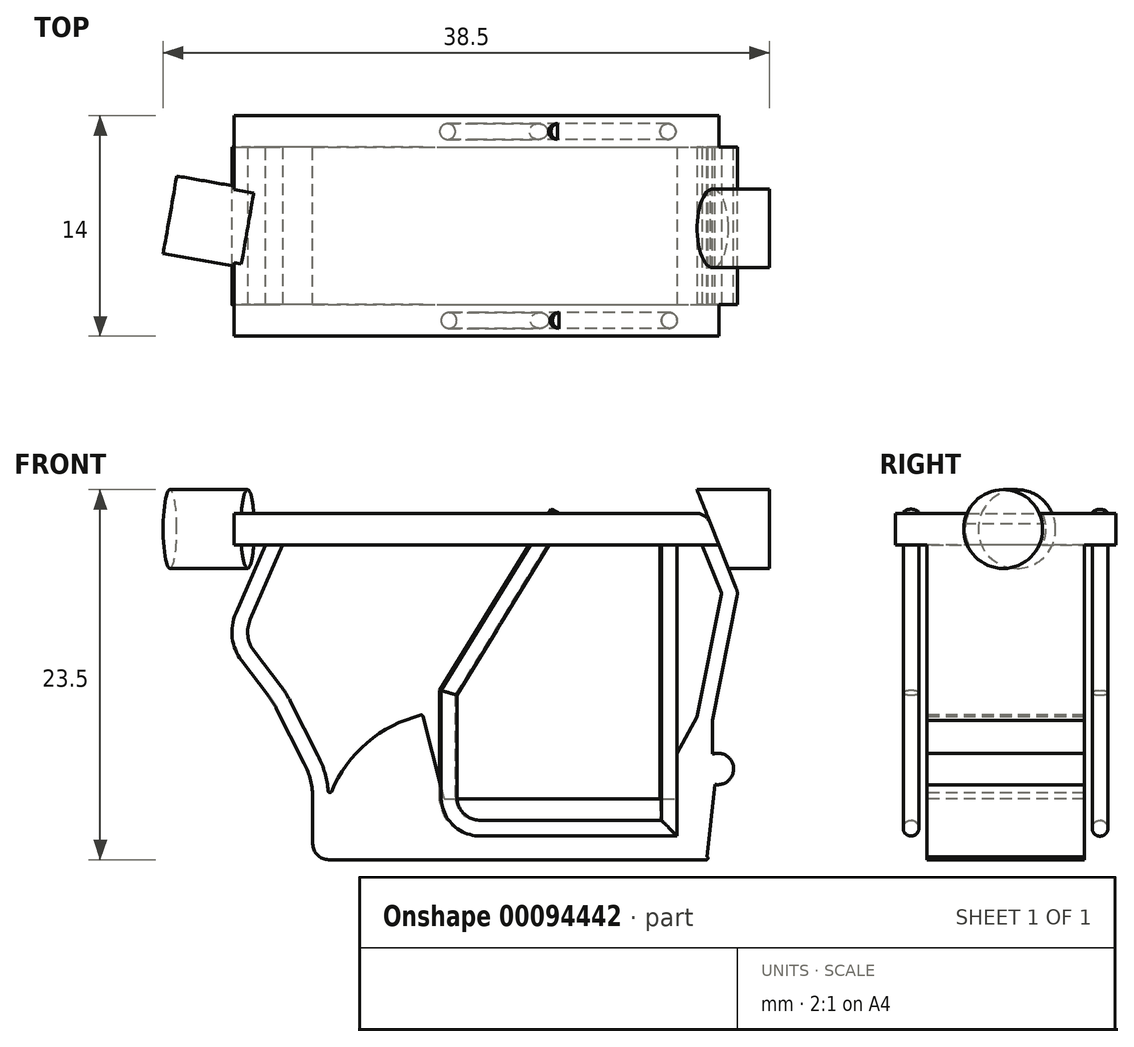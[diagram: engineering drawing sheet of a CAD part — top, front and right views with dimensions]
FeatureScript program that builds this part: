
annotation { "Feature Type Name" : "Feature", "Feature Type Description" : "" }
export const myFeature = defineFeature(function(context is Context, id is Id, definition is map)
    precondition{}
    {
        {
            var Q0;
            Q0=qCreatedBy(makeId("Front.planeOp"),FACE);
            var sketch = newSketch(context, id + "F0", { "sketchPlane" : qUnion([Q0])});
            skLineSegment(sketch, "E0", {"start": v(0, 1) * mm, "end": v(0, 3.86) * mm});
            skLineSegment(sketch, "E1", {"start": v(-4.89, 15.66) * mm, "end": v(-3, 20) * mm});
            skLineSegment(sketch, "E2", {"start": v(-3, 20) * mm, "end": v(-5, 20) * mm});
            skLineSegment(sketch, "E3", {"start": v(-5, 20) * mm, "end": v(-5, 22) * mm});
            skLineSegment(sketch, "E4", {"start": v(-5, 22) * mm, "end": v(24.32, 22) * mm});
            skLineSegment(sketch, "E5", {"start": v(25.25, 21.37) * mm, "end": v(26.9, 17.27) * mm});
            skLineSegment(sketch, "E6", {"start": v(26.94, 16.7) * mm, "end": v(25.4, 8.86) * mm});
            skLineSegment(sketch, "E7", {"start": v(1, 0) * mm, "end": v(25, 0) * mm});
            skLineSegment(sketch, "E8", {"start": v(-0.54, 6.13) * mm, "end": v(-2.32, 9.62) * mm});
            skLineSegment(sketch, "E9", {"start": v(-2.8, 10.39) * mm, "end": v(-4.52, 12.64) * mm});
            skPoint(sketch, "E10.visualSharp", {"position": v(0, 5.06) * mm});
            skArc(sketch, "E10.filletArc", {"start": v(0, 3.86) * mm, "mid": v(-0.14, 5.03) * mm, "end": v(-0.54, 6.13) * mm});
            skPoint(sketch, "E11.visualSharp", {"position": v(-2.52, 10.03) * mm});
            skArc(sketch, "E11.filletArc", {"start": v(-2.32, 9.62) * mm, "mid": v(-2.54, 10.02) * mm, "end": v(-2.8, 10.39) * mm});
            skPoint(sketch, "E12.visualSharp", {"position": v(-5.59, 14.04) * mm});
            skArc(sketch, "E12.filletArc", {"start": v(-4.89, 15.66) * mm, "mid": v(-5.11, 14.1) * mm, "end": v(-4.52, 12.64) * mm});
            skPoint(sketch, "E13.visualSharp", {"position": v(0, 0) * mm});
            skArc(sketch, "E13.filletArc", {"start": v(0, 1) * mm, "mid": v(0.3, 0.3) * mm, "end": v(1, 0) * mm});
            skPoint(sketch, "E14.visualSharp", {"position": v(25, 22) * mm});
            skArc(sketch, "E14.filletArc", {"start": v(25.25, 21.37) * mm, "mid": v(24.88, 21.83) * mm, "end": v(24.32, 22) * mm});
            skPoint(sketch, "E15.visualSharp", {"position": v(27, 17) * mm});
            skArc(sketch, "E15.filletArc", {"start": v(26.94, 16.7) * mm, "mid": v(26.96, 17) * mm, "end": v(26.9, 17.27) * mm});
            skPoint(sketch, "E16.visualSharp", {"position": v(30, 0) * mm});
            skArc(sketch, "E16.filletArc", {"start": v(25, 0) * mm, "mid": v(25.1, 0.08) * mm, "end": v(25.05, 0.2) * mm});
            skLineSegment(sketch, "E17", {"start": v(25.4, 8.86) * mm, "end": v(25.4, 6.7) * mm});
            skLineSegment(sketch, "E18", {"start": v(25.05, 0.2) * mm, "end": v(25.53, 4.78) * mm});
            skArc(sketch, "E19", {"start": v(25.53, 4.78) * mm, "mid": v(26.73, 5.84) * mm, "end": v(25.4, 6.7) * mm});
            skSolve(sketch);
        }
        {
            var Q0;
            Q0=makeQuery(id+"F0.imprint","IMPRINT",FACE,{"disambiguationData":[TD([[makeQuery(id+"F0.imprint","IMPRINT",EDGE,{"derivedFrom":sQuery(id+"F0.wireOp",EDGE,"E0")}),-1.0]])]});
            extrude(context, id + "F1", {"entities" : qUnion([Q0]), "depth" : 10 * mm});
        }
        {
            var Q0;
            Q0=makeQuery(id+"F1.opExtrude","CAP_FACE",FACE,{"disambiguationData":[OSD([sQuery(id+"F0.wireOp",EDGE,"E0"),sQuery(id+"F0.wireOp",EDGE,"E1"),sQuery(id+"F0.wireOp",EDGE,"E2"),sQuery(id+"F0.wireOp",EDGE,"E3"),sQuery(id+"F0.wireOp",EDGE,"E4"),sQuery(id+"F0.wireOp",EDGE,"E5"),sQuery(id+"F0.wireOp",EDGE,"E6"),sQuery(id+"F0.wireOp",EDGE,"E7"),sQuery(id+"F0.wireOp",EDGE,"E8"),sQuery(id+"F0.wireOp",EDGE,"E9"),sQuery(id+"F0.wireOp",EDGE,"E10.filletArc"),sQuery(id+"F0.wireOp",EDGE,"E11.filletArc"),sQuery(id+"F0.wireOp",EDGE,"E12.filletArc"),sQuery(id+"F0.wireOp",EDGE,"E13.filletArc"),sQuery(id+"F0.wireOp",EDGE,"E14.filletArc"),sQuery(id+"F0.wireOp",EDGE,"E15.filletArc"),sQuery(id+"F0.wireOp",EDGE,"E16.filletArc"),sQuery(id+"F0.wireOp",EDGE,"E17"),sQuery(id+"F0.wireOp",EDGE,"E18"),sQuery(id+"F0.wireOp",EDGE,"E19")])],"isStart":false});
            var sketch = newSketch(context, id + "F2", { "sketchPlane" : qUnion([Q0])});
            skLineSegment(sketch, "E20", {"start": v(-5, 20) * mm, "end": v(25.8, 20) * mm});
            skLineSegment(sketch, "E21.0", {"start": v(-3.97, 15.26) * mm, "end": v(-2.08, 19.6) * mm});
            skArc(sketch, "E21.1", {"start": v(-3.97, 15.26) * mm, "mid": v(-4.12, 14.22) * mm, "end": v(-3.73, 13.25) * mm});
            skArc(sketch, "E21.2", {"start": v(0.98, 4.35) * mm, "mid": v(0.77, 5.5) * mm, "end": v(0.35, 6.58) * mm});
            skLineSegment(sketch, "E21.3", {"start": v(0.35, 6.58) * mm, "end": v(-1.43, 10.08) * mm});
            skArc(sketch, "E21.4", {"start": v(-1.43, 10.08) * mm, "mid": v(-1.7, 10.55) * mm, "end": v(-2, 11) * mm});
            skLineSegment(sketch, "E21.5", {"start": v(-2, 11) * mm, "end": v(-3.73, 13.25) * mm});
            skLineSegment(sketch, "E22", {"start": v(-2.08, 19.6) * mm, "end": v(-1.9, 20) * mm});
            skArc(sketch, "E23.0", {"start": v(26.94, 16.7) * mm, "mid": v(26.96, 17) * mm, "end": v(26.9, 17.27) * mm});
            skLineSegment(sketch, "E24.0", {"start": v(25.96, 16.87) * mm, "end": v(24.41, 9.06) * mm});
            skLineSegment(sketch, "E25", {"start": v(25.95, 16.93) * mm, "end": v(24.72, 20) * mm});
            skArc(sketch, "E26.filletArc", {"start": v(25.96, 16.87) * mm, "mid": v(25.96, 16.9) * mm, "end": v(25.95, 16.93) * mm});
            skArc(sketch, "E27", {"start": v(6.88, 9.18) * mm, "mid": v(3.45, 7.42) * mm, "end": v(1.18, 4.32) * mm});
            skLineSegment(sketch, "E28", {"start": v(7, 9.1) * mm, "end": v(8.31, 3.94) * mm});
            skLineSegment(sketch, "E29", {"start": v(23.12, 6.71) * mm, "end": v(24.41, 9.06) * mm});
            skPoint(sketch, "E30.visualSharp", {"position": v(1, 3.86) * mm});
            skArc(sketch, "E30.filletArc", {"start": v(0.98, 4.35) * mm, "mid": v(1.07, 4.26) * mm, "end": v(1.18, 4.32) * mm});
            skPoint(sketch, "E31.visualSharp", {"position": v(6.98, 9.2) * mm});
            skArc(sketch, "E31.filletArc", {"start": v(7, 9.1) * mm, "mid": v(6.95, 9.17) * mm, "end": v(6.88, 9.18) * mm});
            skPoint(sketch, "E32.visualSharp", {"position": v(8.33, 3.86) * mm});
            skArc(sketch, "E32.filletArc", {"start": v(8.31, 3.94) * mm, "mid": v(8.35, 3.89) * mm, "end": v(8.41, 3.86) * mm});
            skLineSegment(sketch, "E33", {"start": v(8.41, 3.86) * mm, "end": v(23.12, 3.86) * mm});
            skLineSegment(sketch, "E34", {"start": v(23.12, 3.86) * mm, "end": v(23.12, 6.71) * mm});
            skSolve(sketch);
        }
        {
            var Q0;
            Q0 = qSketchRegion(id + "F2", true);
            extrude(context, id + "F3", {"entities" : qUnion([Q0]), "operationType" : NewBodyOperationType.REMOVE, "endBound" : BoundingType.THROUGH_ALL, "oppositeDirection" : true, "depth" : 25 * mm});
        }
        {
            var Q0;
            Q0=makeQuery(id+"F1.opExtrude","CAP_EDGE",EDGE,{"disambiguationData":[OSD([sQuery(id+"F0.wireOp",EDGE,"E3")])],"isStart":false});
            cPlane(context, id + "F4", {"entities" : qUnion([Q0]), "cplaneType" : CPlaneType.LINE_ANGLE, "offset" : 150 * mm, "angle" : 350 * degree, "width" : 150 * mm, "height" : 150 * mm});
        }
        {
            var Q0;
            Q0=qCreatedBy(id+"F4.planeOp",FACE);
            var sketch = newSketch(context, id + "F5", { "sketchPlane" : qUnion([Q0])});
            skCircle(sketch, "E35", {"center": v(-5.8, 21) * mm, "radius": 2.5 * mm});
            skSolve(sketch);
        }
        {
            var Q0;
            Q0 = qSketchRegion(id + "F5", true);
            extrude(context, id + "F6", {"entities" : qUnion([Q0]), "operationType" : NewBodyOperationType.ADD, "oppositeDirection" : true, "depth" : 5 * mm});
        }
        {
            var Q0;
            Q0=qCreatedBy(makeId("Right.planeOp"),FACE);
            cPlane(context, id + "F7", {"entities" : qUnion([Q0]), "cplaneType" : CPlaneType.OFFSET, "offset" : 27 * mm, "width" : 150 * mm, "height" : 150 * mm});
        }
        {
            var Q0;
            Q0=qCreatedBy(id+"F7.planeOp",FACE);
            var sketch = newSketch(context, id + "F8", { "sketchPlane" : qUnion([Q0])});
            skEllipticalArc(sketch, "E36.0.0", {});
            skCircle(sketch, "E37", {"center": v(-5.15, 21) * mm, "radius": 2.5 * mm});
            const initialGuessF8  = {"E36.0.0": [-0.0051507684480352305, 0.021, 0, 1, 0.0025, 0.0024620193825305205, 5.123905826452181, 1.1592794807274145]};
            skSetInitialGuess(sketch, initialGuessF8);
            skSolve(sketch);
        }
        {
            var Q0;
            Q0 = qSketchRegion(id + "F8", true);
            var Q1;
            Q1=makeQuery(id+"F1.opExtrude","SWEPT_FACE",FACE,{"disambiguationData":[OSD([sQuery(id+"F0.wireOp",EDGE,"E5")])]});
            extrude(context, id + "F9", {"entities" : qUnion([Q0]), "operationType" : NewBodyOperationType.ADD, "endBound" : BoundingType.UP_TO_SURFACE, "oppositeDirection" : true, "endBoundEntityFace" : qUnion([Q1]), "depth" : 25 * mm, "hasSecondDirection" : true, "secondDirectionOppositeDirection" : false, "secondDirectionDepth" : 2 * mm});
        }
        {
            var Q0;
            Q0=makeQuery(id+"F1.opExtrude","CAP_FACE",FACE,{"disambiguationData":[OSD([sQuery(id+"F0.wireOp",EDGE,"E0"),sQuery(id+"F0.wireOp",EDGE,"E1"),sQuery(id+"F0.wireOp",EDGE,"E2"),sQuery(id+"F0.wireOp",EDGE,"E3"),sQuery(id+"F0.wireOp",EDGE,"E4"),sQuery(id+"F0.wireOp",EDGE,"E5"),sQuery(id+"F0.wireOp",EDGE,"E6"),sQuery(id+"F0.wireOp",EDGE,"E7"),sQuery(id+"F0.wireOp",EDGE,"E8"),sQuery(id+"F0.wireOp",EDGE,"E9"),sQuery(id+"F0.wireOp",EDGE,"E10.filletArc"),sQuery(id+"F0.wireOp",EDGE,"E11.filletArc"),sQuery(id+"F0.wireOp",EDGE,"E12.filletArc"),sQuery(id+"F0.wireOp",EDGE,"E13.filletArc"),sQuery(id+"F0.wireOp",EDGE,"E14.filletArc"),sQuery(id+"F0.wireOp",EDGE,"E15.filletArc"),sQuery(id+"F0.wireOp",EDGE,"E16.filletArc"),sQuery(id+"F0.wireOp",EDGE,"E17"),sQuery(id+"F0.wireOp",EDGE,"E18"),sQuery(id+"F0.wireOp",EDGE,"E19")])],"isStart":false});
            var sketch = newSketch(context, id + "F10", { "sketchPlane" : qUnion([Q0])});
            skLineSegment(sketch, "E38.0", {"start": v(-5, 22) * mm, "end": v(24.32, 22) * mm});
            skLineSegment(sketch, "E39.0", {"start": v(-5, 20) * mm, "end": v(-5, 22) * mm});
            skLineSegment(sketch, "E40.0", {"start": v(-3, 20) * mm, "end": v(-5, 20) * mm});
            skLineSegment(sketch, "E41.0", {"start": v(-1.9, 20) * mm, "end": v(24.72, 20) * mm});
            skArc(sketch, "E42.0", {"start": v(25.25, 21.37) * mm, "mid": v(24.88, 21.83) * mm, "end": v(24.32, 22) * mm});
            skLineSegment(sketch, "E43", {"start": v(-1.9, 20) * mm, "end": v(-3, 20) * mm});
            skLineSegment(sketch, "E44", {"start": v(24.72, 20) * mm, "end": v(25.8, 20) * mm});
            skLineSegment(sketch, "E45", {"start": v(25.8, 20) * mm, "end": v(25.25, 21.37) * mm});
            skSolve(sketch);
        }
        {
            var Q0;
            Q0 = qSketchRegion(id + "F10", true);
            extrude(context, id + "F11", {"entities" : qUnion([Q0]), "operationType" : NewBodyOperationType.ADD, "depth" : 2 * mm, "hasSecondDirection" : true, "secondDirectionOppositeDirection" : true, "secondDirectionDepth" : 12 * mm});
        }
        {
            var Q0;
            Q0=makeQuery(id+"F11.opExtrude","CAP_FACE",FACE,{"disambiguationData":[OSD([sQuery(id+"F10.wireOp",EDGE,"E38.0"),sQuery(id+"F10.wireOp",EDGE,"E39.0"),sQuery(id+"F10.wireOp",EDGE,"E40.0"),sQuery(id+"F10.wireOp",EDGE,"E41.0"),sQuery(id+"F10.wireOp",EDGE,"E42.0"),sQuery(id+"F10.wireOp",EDGE,"E43"),sQuery(id+"F10.wireOp",EDGE,"E44"),sQuery(id+"F10.wireOp",EDGE,"E45")])],"isStart":false});
            cPlane(context, id + "F12", {"entities" : qUnion([Q0]), "cplaneType" : CPlaneType.OFFSET, "offset" : 1 * mm, "oppositeDirection" : true, "width" : 150 * mm, "height" : 150 * mm});
        }
        {
            var Q0;
            Q0=qCreatedBy(id+"F12.planeOp",FACE);
            var sketch = newSketch(context, id + "F13", { "sketchPlane" : qUnion([Q0])});
            skLineSegment(sketch, "E46", {"start": v(15.65, 22) * mm, "end": v(8.65, 10.6) * mm});
            skLineSegment(sketch, "E47", {"start": v(8.65, 10.6) * mm, "end": v(8.65, 4) * mm});
            skLineSegment(sketch, "E48", {"start": v(10.65, 2) * mm, "end": v(22.65, 2) * mm});
            skLineSegment(sketch, "E49", {"start": v(22.65, 2) * mm, "end": v(22.65, 22) * mm});
            skLineSegment(sketch, "E50", {"start": v(8.65, 7.04) * mm, "end": v(22.65, 7.04) * mm});
            skLineSegment(sketch, "E51", {"start": v(15.65, 22) * mm, "end": v(22.65, 22) * mm});
            skPoint(sketch, "E52.visualSharp", {"position": v(8.65, 2) * mm});
            skArc(sketch, "E52.filletArc", {"start": v(8.65, 4) * mm, "mid": v(9.23, 2.59) * mm, "end": v(10.65, 2) * mm});
            skLineSegment(sketch, "E53", {"start": v(12.15, 16.3) * mm, "end": v(22.65, 16.3) * mm});
            skLineSegment(sketch, "E54", {"start": v(9.8, 12.47) * mm, "end": v(22.65, 12.47) * mm});
            skSolve(sketch);
        }
        {
            var Q0;
            Q0=makeQuery(id+"F11.boolean.opBoolean","MERGE",FACE,{"derivedFrom":[makeQuery(id+"F1.opExtrude","SWEPT_FACE",FACE,{"disambiguationData":[OSD([sQuery(id+"F0.wireOp",EDGE,"E4")])]}),makeQuery(id+"F11.opExtrude","SWEPT_FACE",FACE,{"disambiguationData":[OSD([sQuery(id+"F10.wireOp",EDGE,"E38.0")])]})]});
            var sketch = newSketch(context, id + "F14", { "sketchPlane" : qUnion([Q0])});
            skCircle(sketch, "E55", {"center": v(22.65, -11) * mm, "radius": 0.5 * mm});
            skSolve(sketch);
        }
        {
            var Q0;
            Q0=makeQuery(id+"F14.imprint","IMPRINT",FACE,{"disambiguationData":[TD([[makeQuery(id+"F14.imprint","IMPRINT",EDGE,{"derivedFrom":sQuery(id+"F14.wireOp",EDGE,"E55")}),1.0]])]});
            var Q1;
            Q1=sQuery(id+"F13.wireOp",EDGE,"E49");
            var Q2;
            Q2=sQuery(id+"F13.wireOp",EDGE,"E48");
            var Q3;
            Q3=sQuery(id+"F13.wireOp",EDGE,"E52.filletArc");
            var Q4;
            Q4=sQuery(id+"F13.wireOp",EDGE,"E47");
            var Q5;
            Q5=sQuery(id+"F13.wireOp",EDGE,"E46");
            sweep(context, id + "F15", {"operationType" : NewBodyOperationType.ADD, "profiles" : qUnion([Q0]), "path" : qUnion([Q1, Q2, Q3, Q4, Q5])});
        }
        {
            var Q0;
            Q0=makeQuery(id+"F11.opExtrude","CAP_FACE",FACE,{"disambiguationData":[OSD([sQuery(id+"F10.wireOp",EDGE,"E38.0"),sQuery(id+"F10.wireOp",EDGE,"E39.0"),sQuery(id+"F10.wireOp",EDGE,"E40.0"),sQuery(id+"F10.wireOp",EDGE,"E41.0"),sQuery(id+"F10.wireOp",EDGE,"E42.0"),sQuery(id+"F10.wireOp",EDGE,"E43"),sQuery(id+"F10.wireOp",EDGE,"E44"),sQuery(id+"F10.wireOp",EDGE,"E45")])],"isStart":true});
            cPlane(context, id + "F16", {"entities" : qUnion([Q0]), "cplaneType" : CPlaneType.OFFSET, "offset" : 1 * mm, "oppositeDirection" : true, "width" : 150 * mm, "height" : 150 * mm});
        }
        {
            var Q0;
            Q0=qCreatedBy(id+"F16.planeOp",FACE);
            var sketch = newSketch(context, id + "F17", { "sketchPlane" : qUnion([Q0])});
            skLineSegment(sketch, "E56", {"start": v(-8.56, 10.6) * mm, "end": v(-8.56, 4) * mm});
            skPoint(sketch, "E57.visualSharp", {"position": v(-8.56, 2) * mm});
            skLineSegment(sketch, "E58.MirrorCS", {"start": v(-8.56, 7.04) * mm, "end": v(-22.56, 7.04) * mm});
            skLineSegment(sketch, "E59.MirrorCS", {"start": v(-9.7, 12.47) * mm, "end": v(-22.56, 12.47) * mm});
            skLineSegment(sketch, "E60.MirrorCS", {"start": v(-15.56, 22) * mm, "end": v(-8.56, 10.6) * mm});
            skLineSegment(sketch, "E61.MirrorCS", {"start": v(-12.06, 16.3) * mm, "end": v(-22.56, 16.3) * mm});
            skLineSegment(sketch, "E62.MirrorCS", {"start": v(-15.56, 22) * mm, "end": v(-22.56, 22) * mm});
            skLineSegment(sketch, "E63.MirrorCS", {"start": v(-22.56, 2) * mm, "end": v(-22.56, 22) * mm});
            skLineSegment(sketch, "E64.MirrorCS", {"start": v(-10.56, 2) * mm, "end": v(-22.56, 2) * mm});
            skArc(sketch, "E65", {"start": v(-10.56, 2) * mm, "mid": v(-9.14, 2.58) * mm, "end": v(-8.56, 4) * mm});
            skSolve(sketch);
        }
        {
            var Q0;
            Q0=makeQuery(id+"F11.boolean.opBoolean","MERGE",FACE,{"derivedFrom":[makeQuery(id+"F1.opExtrude","SWEPT_FACE",FACE,{"disambiguationData":[OSD([sQuery(id+"F0.wireOp",EDGE,"E4")])]}),makeQuery(id+"F11.opExtrude","SWEPT_FACE",FACE,{"disambiguationData":[OSD([sQuery(id+"F10.wireOp",EDGE,"E38.0")])]})]});
            var sketch = newSketch(context, id + "F18", { "sketchPlane" : qUnion([Q0])});
            skCircle(sketch, "E66", {"center": v(22.56, 1) * mm, "radius": 0.5 * mm});
            skSolve(sketch);
        }
        {
            var Q0;
            Q0=makeQuery(id+"F18.imprint","IMPRINT",FACE,{"disambiguationData":[TD([[makeQuery(id+"F18.imprint","IMPRINT",EDGE,{"derivedFrom":sQuery(id+"F18.wireOp",EDGE,"E66")}),1.0]])]});
            var Q1;
            Q1=sQuery(id+"F17.wireOp",EDGE,"E63.MirrorCS");
            var Q2;
            Q2=sQuery(id+"F17.wireOp",EDGE,"E60.MirrorCS");
            var Q3;
            Q3=sQuery(id+"F17.wireOp",EDGE,"E64.MirrorCS");
            var Q4;
            Q4=sQuery(id+"F17.wireOp",EDGE,"E65");
            var Q5;
            Q5=sQuery(id+"F17.wireOp",EDGE,"E56");
            sweep(context, id + "F19", {"operationType" : NewBodyOperationType.ADD, "profiles" : qUnion([Q0]), "path" : qUnion([Q1, Q2, Q3, Q4, Q5])});
        }
    });
